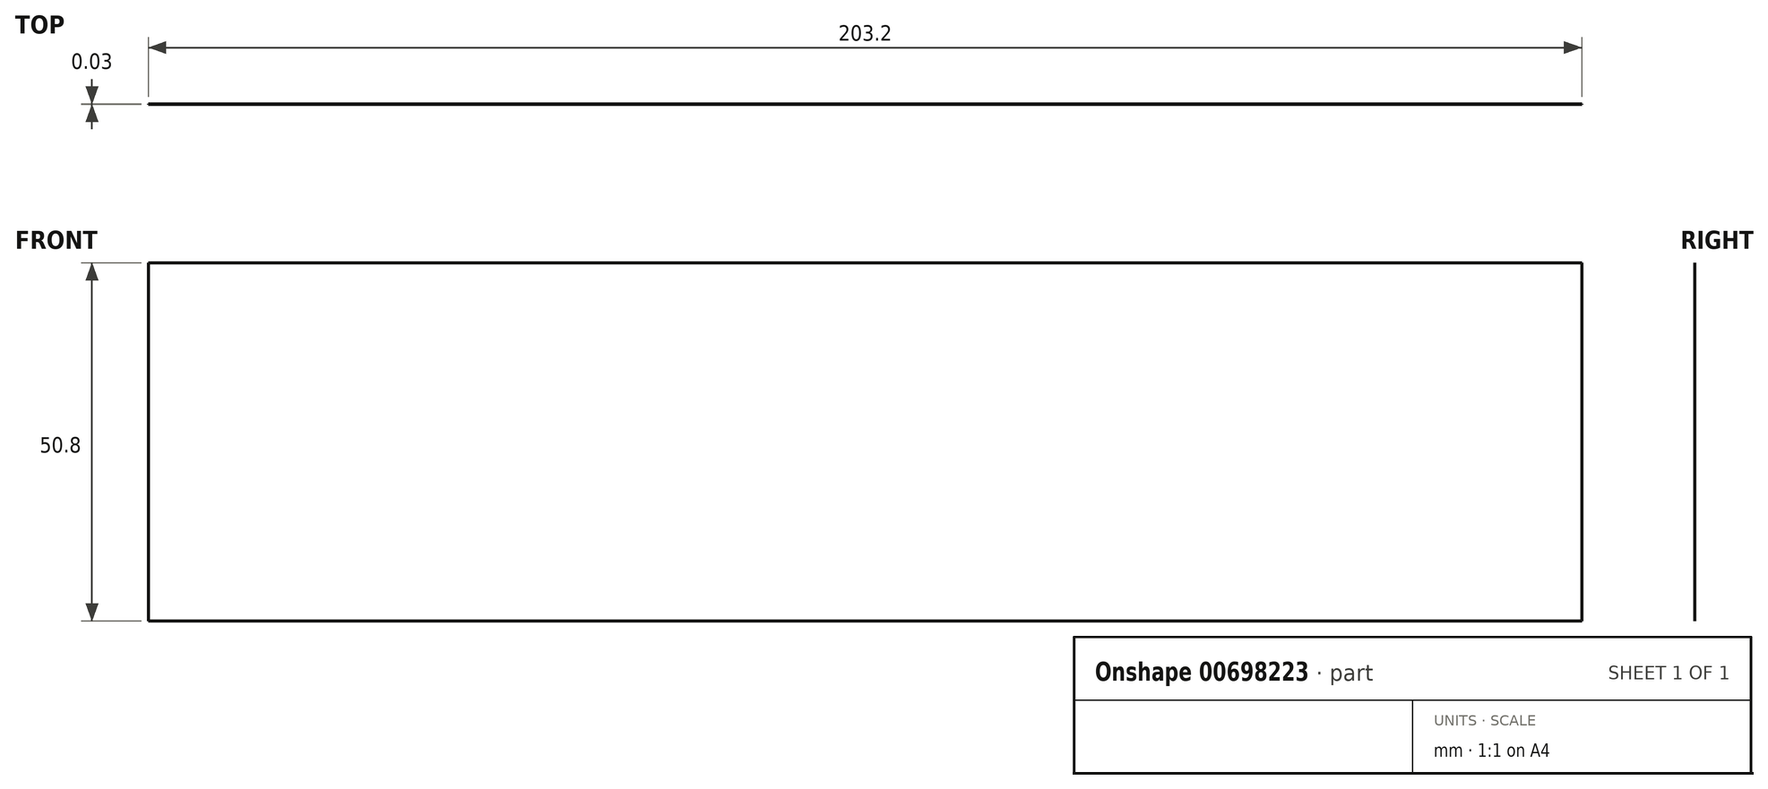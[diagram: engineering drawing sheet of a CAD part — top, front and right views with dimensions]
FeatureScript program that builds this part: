
annotation { "Feature Type Name" : "Feature", "Feature Type Description" : "" }
export const myFeature = defineFeature(function(context is Context, id is Id, definition is map)
    precondition{}
    {
        {
            var Q0;
            Q0=qCreatedBy(makeId("Front.planeOp"),FACE);
            var sketch = newSketch(context, id + "F0", { "sketchPlane" : qUnion([Q0])});
            skLineSegment(sketch, "E0.bottom", {"start": v(-157.79, 19.92) * mm, "end": v(45.41, 19.92) * mm});
            skLineSegment(sketch, "E0.top", {"start": v(-157.79, -30.88) * mm, "end": v(45.41, -30.88) * mm});
            skLineSegment(sketch, "E0.left", {"start": v(-157.79, 19.92) * mm, "end": v(-157.79, -30.88) * mm});
            skLineSegment(sketch, "E0.right", {"start": v(45.41, 19.92) * mm, "end": v(45.41, -30.88) * mm});
            skSolve(sketch);
        }
        {
            var Q0;
            Q0=makeQuery(id+"F0.imprint","IMPRINT",FACE,{"disambiguationData":[TD([[makeQuery(id+"F0.imprint","IMPRINT",EDGE,{"derivedFrom":sQuery(id+"F0.wireOp",EDGE,"E0.bottom")}),-1.0]])]});
            extrude(context, id + "F1", {"entities" : qUnion([Q0]), "depth" : 3 / 101.6 * mm, "offsetDistance" : 25.4 * mm});
        }
    });
